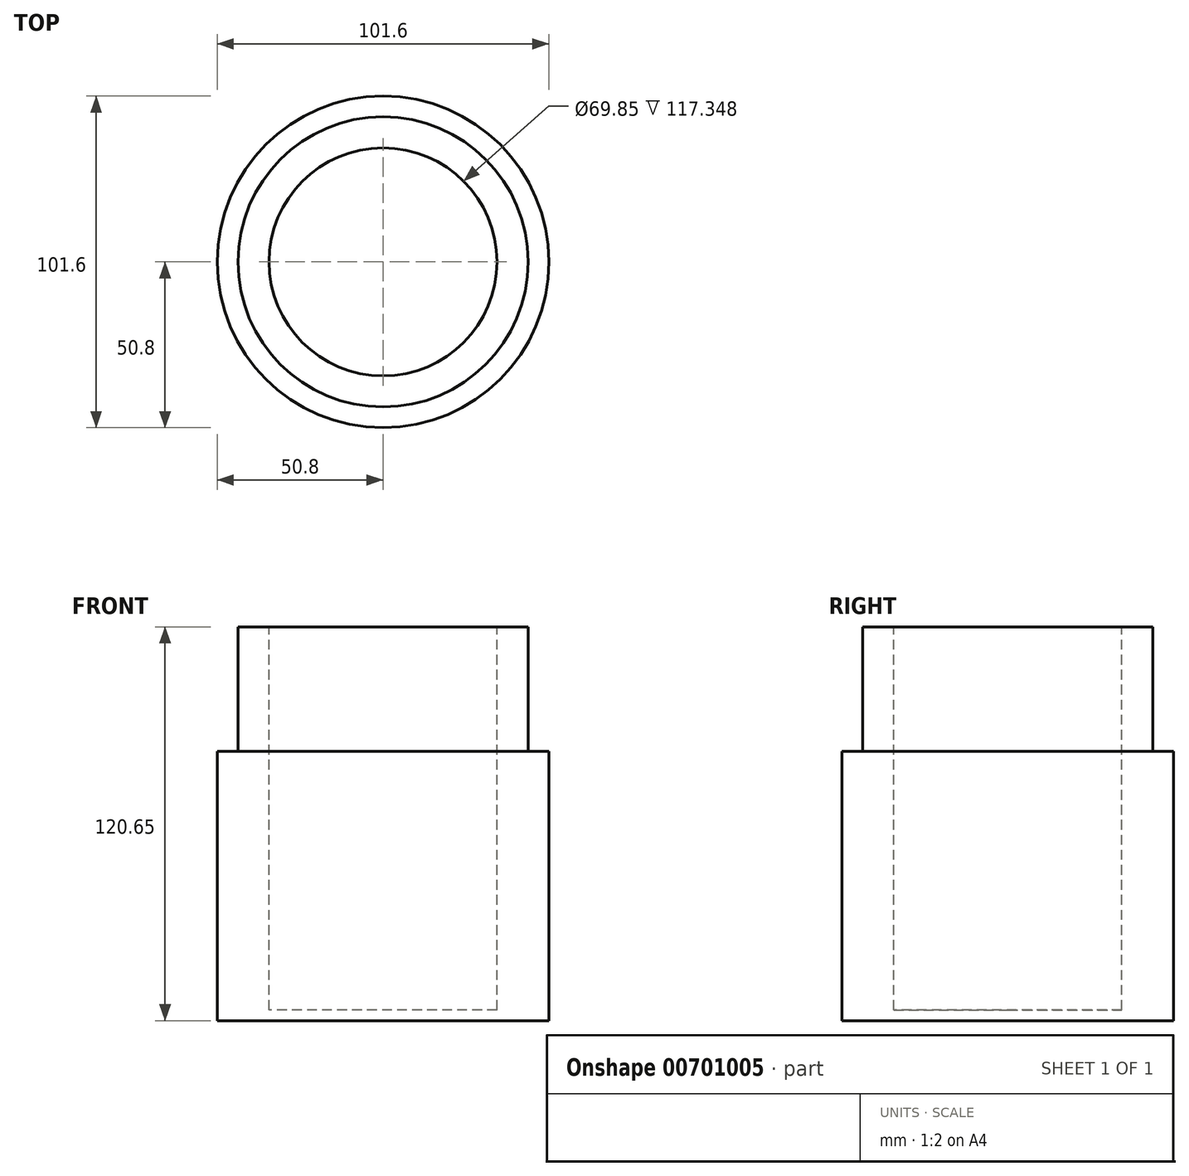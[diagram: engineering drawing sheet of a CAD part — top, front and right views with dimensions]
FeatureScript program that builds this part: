
annotation { "Feature Type Name" : "Feature", "Feature Type Description" : "" }
export const myFeature = defineFeature(function(context is Context, id is Id, definition is map)
    precondition{}
    {
        {
            var Q0;
            Q0=qCreatedBy(makeId("Top.planeOp"),FACE);
            var sketch = newSketch(context, id + "F0", { "sketchPlane" : qUnion([Q0])});
            skCircle(sketch, "E0", {"center": v(0, 0) * mm, "radius": 50.8 * mm});
            skSolve(sketch);
        }
        {
            var Q0;
            Q0 = qSketchRegion(id + "F0", true);
            extrude(context, id + "F1", {"entities" : qUnion([Q0]), "depth" : 82.55 * mm, "offsetDistance" : 25.4 * mm});
        }
        {
            var Q0;
            Q0=makeQuery(id+"F1.opExtrude","CAP_FACE",FACE,{"disambiguationData":[OSD([sQuery(id+"F0.wireOp",EDGE,"E0")])],"isStart":false});
            var sketch = newSketch(context, id + "F2", { "sketchPlane" : qUnion([Q0])});
            skCircle(sketch, "E1", {"center": v(0, 0) * mm, "radius": 44.45 * mm});
            skSolve(sketch);
        }
        {
            var Q0;
            Q0=makeQuery(id+"F2.imprint","IMPRINT",FACE,{"disambiguationData":[TD([[makeQuery(id+"F2.imprint","IMPRINT",EDGE,{"derivedFrom":sQuery(id+"F2.wireOp",EDGE,"E1")}),1.0]])]});
            extrude(context, id + "F3", {"entities" : qUnion([Q0]), "operationType" : NewBodyOperationType.ADD, "depth" : 38.1 * mm, "offsetDistance" : 25.4 * mm});
        }
        {
            var Q0;
            Q0=makeQuery(id+"F3.opExtrude","CAP_FACE",FACE,{"disambiguationData":[OSD([sQuery(id+"F2.wireOp",EDGE,"E1")])],"isStart":false});
            var sketch = newSketch(context, id + "F4", { "sketchPlane" : qUnion([Q0])});
            skCircle(sketch, "E2", {"center": v(0, 0) * mm, "radius": 34.93 * mm});
            skSolve(sketch);
        }
        {
            var Q0;
            Q0=makeQuery(id+"F4.imprint","IMPRINT",FACE,{"disambiguationData":[TD([[makeQuery(id+"F4.imprint","IMPRINT",EDGE,{"derivedFrom":sQuery(id+"F4.wireOp",EDGE,"E2")}),1.0]])]});
            extrude(context, id + "F5", {"entities" : qUnion([Q0]), "operationType" : NewBodyOperationType.REMOVE, "oppositeDirection" : true, "depth" : 117.35 * mm, "offsetDistance" : 25.4 * mm});
        }
    });
